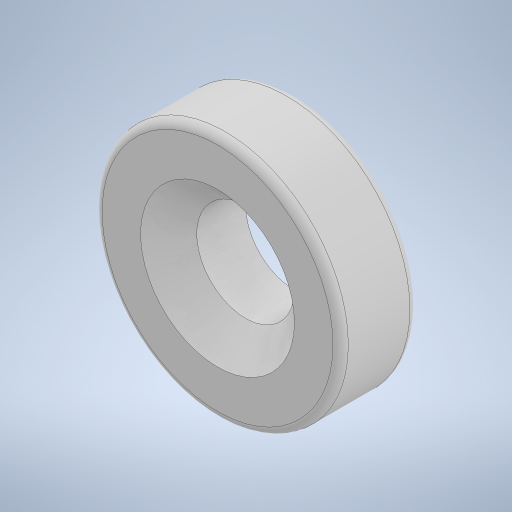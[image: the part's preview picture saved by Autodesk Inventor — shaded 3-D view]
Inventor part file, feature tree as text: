
AUTODESK INVENTOR PART (.ipt)
format: ipt  version: 2023 (Build 270158000, 158)  size: 251,904 bytes
history: native  units: mm
features: sketch x1, extrude x1, hole x1, fillet x1
ambient origin geometry x8: Origin, YZ Plane, XZ Plane, XY Plane, X Axis, Y Axis, Z Axis, Center Point
bodies: Solid1 (feature_tree)
feature tree (4):
  sketch  "Sketch1"  dims[d0=16.0mm d2=5.0mm d3=0.0mm d4=6.35mm d5=6.0mm d6=10.0mm d7=2.0mm d8=90.0deg d9=8.0mm d10=20.594885mm d11=0.5mm]
  extrude  "Extrusion1"  Depth=5.0mm TaperAngle=0.0deg
  hole  "Hole1"  [1 undecoded]
  fillet  "Fillet1"  [1 undecoded]
note: 2 required parameter values undecoded (feature->parameter linkage not recoverable at this tier; creation-order binding heuristic only, values carry confidence <= 0.55)
